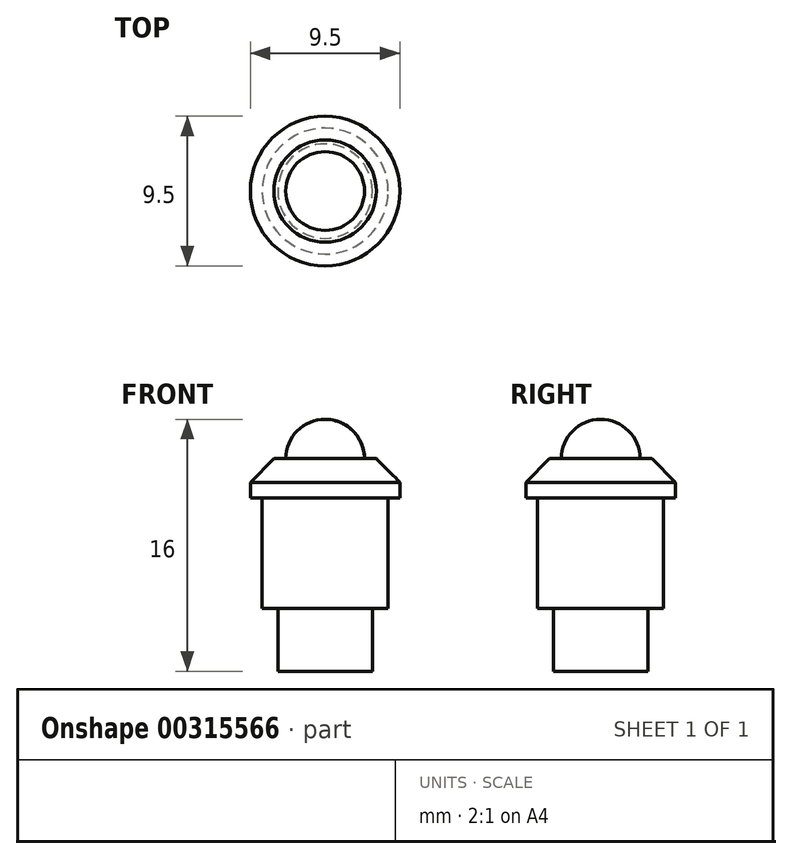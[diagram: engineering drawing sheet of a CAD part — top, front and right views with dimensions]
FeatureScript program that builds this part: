
annotation { "Feature Type Name" : "Feature", "Feature Type Description" : "" }
export const myFeature = defineFeature(function(context is Context, id is Id, definition is map)
    precondition{}
    {
        {
            var Q0;
            Q0=qCreatedBy(makeId("Front.planeOp"),FACE);
            var sketch = newSketch(context, id + "F0", { "sketchPlane" : qUnion([Q0])});
            skArc(sketch, "E0", {"start": v(2.5, 2.5) * mm, "mid": v(1.77, 4.27) * mm, "end": v(0, 5) * mm});
            skLineSegment(sketch, "E1", {"start": v(4.75, 1) * mm, "end": v(4.75, 0) * mm});
            skLineSegment(sketch, "E2", {"start": v(4.75, 0) * mm, "end": v(4, 0) * mm});
            skLineSegment(sketch, "E3", {"start": v(4, 0) * mm, "end": v(4, -7) * mm});
            skLineSegment(sketch, "E4", {"start": v(4, -7) * mm, "end": v(3, -7) * mm});
            skLineSegment(sketch, "E5", {"start": v(0, -7) * mm, "end": v(0, 5) * mm});
            skLineSegment(sketch, "E6", {"start": v(2.5, 2.5) * mm, "end": v(3.25, 2.5) * mm});
            skLineSegment(sketch, "E7", {"start": v(3.25, 2.5) * mm, "end": v(4.75, 1) * mm});
            skLineSegment(sketch, "E8", {"start": v(3, -7) * mm, "end": v(3, -11) * mm});
            skLineSegment(sketch, "E9", {"start": v(3, -11) * mm, "end": v(0, -11) * mm});
            skLineSegment(sketch, "E10", {"start": v(0, -11) * mm, "end": v(0, -7) * mm});
            skLineSegment(sketch, "E11", {"start": v(0, 5) * mm, "end": v(0, -12.36) * mm, "construction": true});
            skSolve(sketch);
        }
        {
            var Q0;
            Q0 = qSketchRegion(id + "F0", true);
            var Q1;
            Q1=sQuery(id+"F0.wireOp",EDGE,"E11");
            revolve(context, id + "F1", {"entities" : qUnion([Q0]), "axis" : qUnion([Q1]), "revolveType" : RevolveType.FULL});
        }
    });
